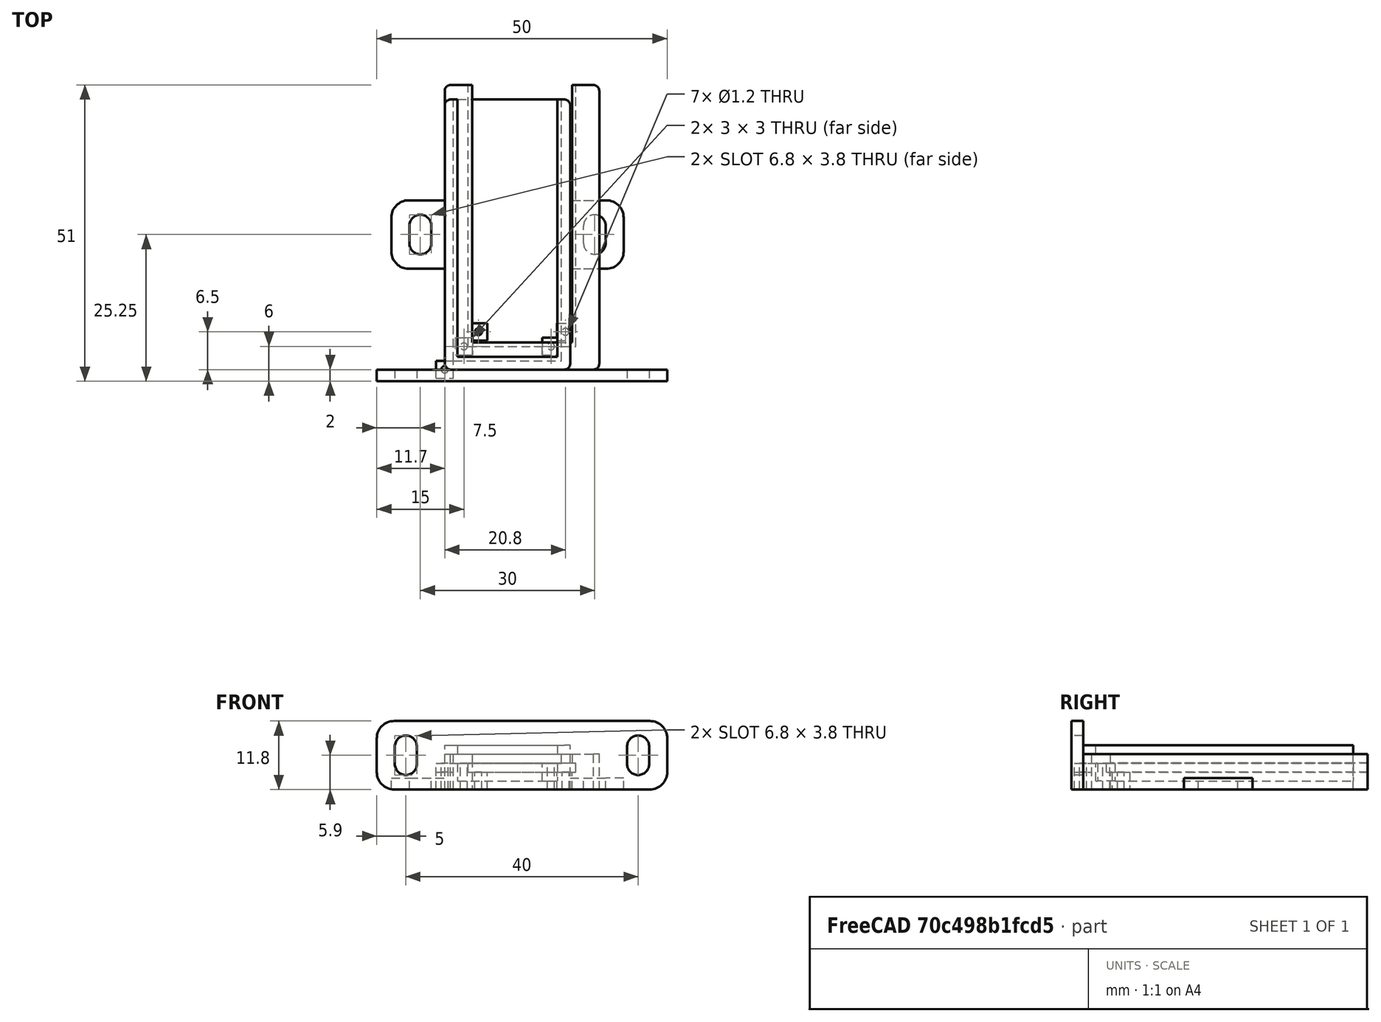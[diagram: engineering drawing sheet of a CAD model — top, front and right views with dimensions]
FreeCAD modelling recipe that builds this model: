
FCSTD DOCUMENT  (FreeCAD 0.19R)
Label: arduino_nano
License: FreeArt
LicenseURL: http://artlibre.org/licence/lal
objects: Part::Box×8, Part::MultiFuse×7, Part::Cut×7, Part::FeaturePython×4, App::Part×3, Part::Fillet×2, Part::Cylinder×2, Part::Feature×2, Spreadsheet::Sheet×1
note: 28 computed .brp shape members not serialized (recipe doc carries the construction recipe); baked Part::Feature solids carry a one-line shape summary decoded from their .brp

FEATURE [Spreadsheet::Sheet] Spreadsheet  label="p"
  cells = A1=pcb_x; B1(pcb_x)=18.6; A2=pcb_y; B2(pcb_y)=45; A3=pcb_z; B3(pcb_z)=1.6; A4=pcb_under; B4(pcb_under)=3; A5=pcb_under_vertical; B5(pcb_under_vertical)=3; A6=side_wall; B6(side_wall)=1.5; A7=side_wall_vertical; B7(side_wall_vertical)=4; A8=pcb_side_lane; B8(pcb_side_lane)=0.7; A9=bottom_wall; B9(bottom_wall)=1.5; A10=pcb_above; B10(pcb_above)=1.5; A11=hole_dist_x; B11(hole_dist_x)=15; A12=hole_r; B12(hole_r)=0.6; A13=hole_off_y; B13(hole_off_y)=2.5; A14=hole_stand_size; B14(hole_stand_size)=3
FEATURE [Part::Box] Box  label="external cube"
  AttacherType = Attacher::AttachEngine3D
  Height = 7.6
  Length = 21.6
  Width = 46.5
  expr: Length = <<p>>.pcb_x + 2 * <<p>>.side_wall
  expr: Width = <<p>>.pcb_y + <<p>>.side_wall
  expr: Height = <<p>>.bottom_wall + <<p>>.pcb_under + <<p>>.pcb_z + <<p>>.pcb_above
FEATURE [Part::Box] Box006  label="internal cube"
  AttacherType = Attacher::AttachEngine3D
  Height = 6.1
  Length = 17.2
  Placement = pos=(2.2,2.2,1.5) rot=(0,0,1;0rad)
  Width = 45.1
  expr: Length = <<p>>.pcb_x - 2 * <<p>>.pcb_side_lane
  expr: Width = <<p>>.pcb_y - 2 * <<p>>.pcb_side_lane + <<p>>.side_wall
  expr: Height = <<p>>.pcb_under + <<p>>.pcb_z + <<p>>.pcb_above
  expr: .Placement.Base.z = <<p>>.bottom_wall
  expr: .Placement.Base.x = <<p>>.side_wall + <<p>>.pcb_side_lane
  expr: .Placement.Base.y = <<p>>.side_wall + <<p>>.pcb_side_lane
FEATURE [Part::Box] Box007  label="pcb extract cube"
  AttacherType = Attacher::AttachEngine3D
  Height = 1.6
  Length = 18.6
  Placement = pos=(1.5,1.5,4.5) rot=(0,0,1;0rad)
  Width = 45
  expr: Height = <<p>>.pcb_z
  expr: .Placement.Base.z = <<p>>.bottom_wall + <<p>>.pcb_under
  expr: Width = <<p>>.pcb_y
  expr: Length = <<p>>.pcb_x
  expr: .Placement.Base.x = <<p>>.side_wall
  expr: .Placement.Base.y = <<p>>.side_wall
FEATURE [Part::MultiFuse] Fusion  label="extract fusion"
  Shapes = -> [Box006,Box007]
FEATURE [Part::Fillet] Fillet  label="external fillet"
  Base = -> Box
  Edges = 4 edges r=1: [Edge1,Edge3,Edge5,Edge7]
FEATURE [Part::Cylinder] Cylinder  label="hole"
  Angle = 360
  AttacherType = Attacher::AttachEngine3D
  Height = 10
  Radius = 0.6
  expr: Radius = <<p>>.hole_r
FEATURE [Part::Box] Box008  label="stand"
  AttacherType = Attacher::AttachEngine3D
  Height = 4.5
  Length = 3
  Placement = pos=(-1.5,-1.5,0) rot=(0,0,1;0rad)
  Width = 3
  expr: .Placement.Base.y = -<<p>>.hole_stand_size / 2
  expr: .Placement.Base.x = -<<p>>.hole_stand_size / 2
  expr: Width = <<p>>.hole_stand_size
  expr: Length = <<p>>.hole_stand_size
  expr: Height = <<p>>.pcb_under + <<p>>.bottom_wall
FEATURE [Part::FeaturePython] Array  label="hole array"  # Draft array (typed FeaturePython)
  Angle = 360
  ArrayType = 0
  Axis = (0,0,1)
  Base = -> Box008
  Center = (0,0,0)
  Count = 2
  ExpandArray = false
  Fuse = false
  IntervalAxis = (0,0,0)
  IntervalX = (15,0,0)
  IntervalY = (0,1,0)
  IntervalZ = (0,0,100)
  NumberCircles = 3
  NumberPolar = 5
  NumberX = 2
  NumberY = 1
  NumberZ = 1
  Placement = pos=(3.3,4,0) rot=(0,0,1;0rad)
  PlacementList = 2 placements: [(-1.5,-1.5,0),(13.5,-1.5,0)]
  RadialDistance = 50
  ScaleList = (2) [(1,1,1),(1,1,1)]
  Symmetry = 1
  TangentialDistance = 25
  expr: .IntervalX.x = Spreadsheet.hole_dist_x
  expr: .Placement.Base.x = (2 * <<p>>.side_wall + <<p>>.pcb_x - Spreadsheet.hole_dist_x) / 2
  expr: .Placement.Base.y = Spreadsheet.hole_off_y + <<p>>.side_wall
FEATURE [Part::Cut] Cut003002  label="stand hole cut"
  Base = -> Box008
  Tool = -> Cylinder
FEATURE [Part::FeaturePython] Array001  label="hole array001"  # Draft array (typed FeaturePython)
  Angle = 360
  ArrayType = 0
  Axis = (0,0,1)
  Base = -> Cylinder
  Center = (0,0,0)
  Count = 2
  ExpandArray = false
  Fuse = false
  IntervalAxis = (0,0,0)
  IntervalX = (15,0,0)
  IntervalY = (0,1,0)
  IntervalZ = (0,0,100)
  NumberCircles = 3
  NumberPolar = 5
  NumberX = 2
  NumberY = 1
  NumberZ = 1
  Placement = pos=(3.3,4,0) rot=(0,0,1;0rad)
  PlacementList = 2 placements: [(0,0,0),(15,0,0)]
  RadialDistance = 50
  ScaleList = (2) [(1,1,1),(1,1,1)]
  Symmetry = 1
  TangentialDistance = 25
  expr: .Placement.Base.y = Spreadsheet.hole_off_y + <<p>>.side_wall
  expr: .Placement.Base.x = (2 * <<p>>.side_wall + <<p>>.pcb_x - Spreadsheet.hole_dist_x) / 2
  expr: .IntervalX.x = Spreadsheet.hole_dist_x
FEATURE [Part::Feature] Cut003001  label="attach plane x dir001"
  Placement = pos=(-9.2,17.35,0) rot=(0,0,1;0rad)
  shape: bbox 40 x 11.8 x 2 mm, 18 faces (baked)
FEATURE [Part::MultiFuse] Fusion001  label="body fusion"
  Shapes = -> [Fillet,Cut003001]
FEATURE [Part::Cut] Cut  label="body cut003"
  Base = -> Fusion001
  Tool = -> Fusion
FEATURE [Part::MultiFuse] Fusion002  label="body fusion003"
  Shapes = -> [Array,Cut]
FEATURE [Part::Cut] Cut003003  label="body cut"
  Base = -> Fusion002
  Tool = -> Array001
FEATURE [App::Part] Part  label="arduino nano pcb box part"
  Group = -> [Box,Fillet,Fusion001,Fusion,Box007,Box006,Cut,Cylinder,Box008,Cut003002,Array,Fusion002,Array001,Cut003003]
  Origin = -> Origin
FEATURE [Part::Box] Box009  label="external cube001"
  AttacherType = Attacher::AttachEngine3D
  Height = 6.1
  Length = 26.6
  Width = 49
  expr: Height = <<p>>.pcb_under_vertical + <<p>>.pcb_z + <<p>>.pcb_above
  expr: Width = <<p>>.pcb_y + <<p>>.side_wall_vertical
  expr: Length = <<p>>.pcb_x + 2 * <<p>>.side_wall_vertical
FEATURE [Part::Cylinder] Cylinder001  label="hole001"
  Angle = 360
  AttacherType = Attacher::AttachEngine3D
  Height = 3
  Radius = 0.6
  expr: Radius = <<p>>.hole_r
  expr: Height = <<p>>.pcb_under_vertical
FEATURE [Part::Fillet] Fillet001  label="external fillet001"
  Base = -> Box009
  Edges = 4 edges r=1: [Edge1,Edge3,Edge5,Edge7]
FEATURE [Part::Box] Box010  label="pcb extract cube001"
  AttacherType = Attacher::AttachEngine3D
  Height = 1.6
  Length = 18.6
  Placement = pos=(4,4,3) rot=(0,0,1;0rad)
  Width = 45
  expr: .Placement.Base.y = <<p>>.side_wall_vertical
  expr: .Placement.Base.x = <<p>>.side_wall_vertical
  expr: Length = <<p>>.pcb_x
  expr: Width = <<p>>.pcb_y
  expr: .Placement.Base.z = <<p>>.pcb_under_vertical
  expr: Height = <<p>>.pcb_z
FEATURE [Part::FeaturePython] Array002  label="hole array002"  # Draft array (typed FeaturePython)
  Angle = 360
  ArrayType = 0
  Axis = (0,0,1)
  Base = -> Cylinder001
  Center = (0,0,0)
  Count = 2
  ExpandArray = false
  Fuse = false
  IntervalAxis = (0,0,0)
  IntervalX = (15,0,0)
  IntervalY = (0,1,0)
  IntervalZ = (0,0,100)
  NumberCircles = 3
  NumberPolar = 5
  NumberX = 2
  NumberY = 1
  NumberZ = 1
  Placement = pos=(5.8,6.5,0) rot=(0,0,1;0rad)
  PlacementList = 2 placements: [(0,0,0),(15,0,0)]
  RadialDistance = 50
  ScaleList = (2) [(1,1,1),(1,1,1)]
  Symmetry = 1
  TangentialDistance = 25
  expr: .IntervalX.x = Spreadsheet.hole_dist_x
  expr: .Placement.Base.x = (2 * <<p>>.side_wall_vertical + <<p>>.pcb_x - <<p>>.hole_dist_x) / 2
  expr: .Placement.Base.y = <<p>>.hole_off_y + <<p>>.side_wall_vertical
FEATURE [Part::Box] Box011  label="internal cube001"
  AttacherType = Attacher::AttachEngine3D
  Height = 6.1
  Length = 17.2
  Placement = pos=(4.7,4.7,0) rot=(0,0,1;0rad)
  Width = 47.6
  expr: .Placement.Base.y = <<p>>.side_wall_vertical + <<p>>.pcb_side_lane
  expr: .Placement.Base.x = <<p>>.side_wall_vertical + <<p>>.pcb_side_lane
  expr: Height = <<p>>.pcb_under_vertical + <<p>>.pcb_z + <<p>>.pcb_above
  expr: Width = <<p>>.pcb_y - 2 * <<p>>.pcb_side_lane + <<p>>.side_wall_vertical
  expr: Length = <<p>>.pcb_x - 2 * <<p>>.pcb_side_lane
FEATURE [Part::MultiFuse] Fusion003  label="extract fusion001"
  Shapes = -> [Box011,Box010]
FEATURE [Part::Box] Box012  label="stand001"
  AttacherType = Attacher::AttachEngine3D
  Height = 3
  Length = 3
  Placement = pos=(-1.5,-1.5,0) rot=(0,0,1;0rad)
  Width = 3
  expr: Height = <<p>>.pcb_under_vertical
  expr: Length = <<p>>.hole_stand_size
  expr: Width = <<p>>.hole_stand_size
  expr: .Placement.Base.x = -<<p>>.hole_stand_size / 2
  expr: .Placement.Base.y = -<<p>>.hole_stand_size / 2
FEATURE [Part::FeaturePython] Array003  label="hole array003"  # Draft array (typed FeaturePython)
  Angle = 360
  ArrayType = 0
  Axis = (0,0,1)
  Base = -> Box012
  Center = (0,0,0)
  Count = 2
  ExpandArray = false
  Fuse = false
  IntervalAxis = (0,0,0)
  IntervalX = (15,0,0)
  IntervalY = (0,1,0)
  IntervalZ = (0,0,100)
  NumberCircles = 3
  NumberPolar = 5
  NumberX = 2
  NumberY = 1
  NumberZ = 1
  Placement = pos=(5.8,6.5,0) rot=(0,0,1;0rad)
  PlacementList = 2 placements: [(-1.5,-1.5,0),(13.5,-1.5,0)]
  RadialDistance = 50
  ScaleList = (2) [(1,1,1),(1,1,1)]
  Symmetry = 1
  TangentialDistance = 25
  expr: .Placement.Base.y = <<p>>.hole_off_y + <<p>>.side_wall_vertical
  expr: .Placement.Base.x = (2 * <<p>>.side_wall_vertical + <<p>>.pcb_x - <<p>>.hole_dist_x) / 2
  expr: .IntervalX.x = Spreadsheet.hole_dist_x
FEATURE [Part::Feature] Body002  label="attach plane x rotated dir001"
  Placement = pos=(-11.7,0,0) rot=(1,0,0;1.5708rad)
  shape: bbox 50 x 2 x 11.8 mm, 18 faces (baked)
FEATURE [Part::MultiFuse] Fusion004  label="body fusion001"
  Shapes = -> [Fillet001,Body002]
FEATURE [Part::Cut] Cut003006  label="body cut002"
  Base = -> Fusion004
  Tool = -> Fusion003
FEATURE [Part::MultiFuse] Fusion005  label="body fusion002"
  Shapes = -> [Array003,Cut003006]
FEATURE [Part::Cut] Cut003005  label="body cut001"
  Base = -> Fusion005
  Tool = -> Array002
FEATURE [App::Part] Part001  label="arduino nano vertical pcb box part"
  Group = -> [Box009,Fillet001,Fusion004,Fusion003,Box010,Box011,Cut003006,Cylinder001,Box012,Array003,Fusion005,Array002,Cut003005]
  Origin = -> Origin001
FEATURE [Part::Cut] Cut003007  label="body cut004"
  Base = -> Fillet
  Tool = -> Fusion
FEATURE [Part::MultiFuse] Fusion006  label="body fusion004"
  Shapes = -> [Array,Cut003007]
FEATURE [Part::Cut] Cut003008  label="body cut005"
  Base = -> Fusion006
  Tool = -> Array001
FEATURE [App::Part] Part002  label="arduino nano pcb box part no attachment"
  Group = -> [Cut003008]
  Origin = -> Origin002
